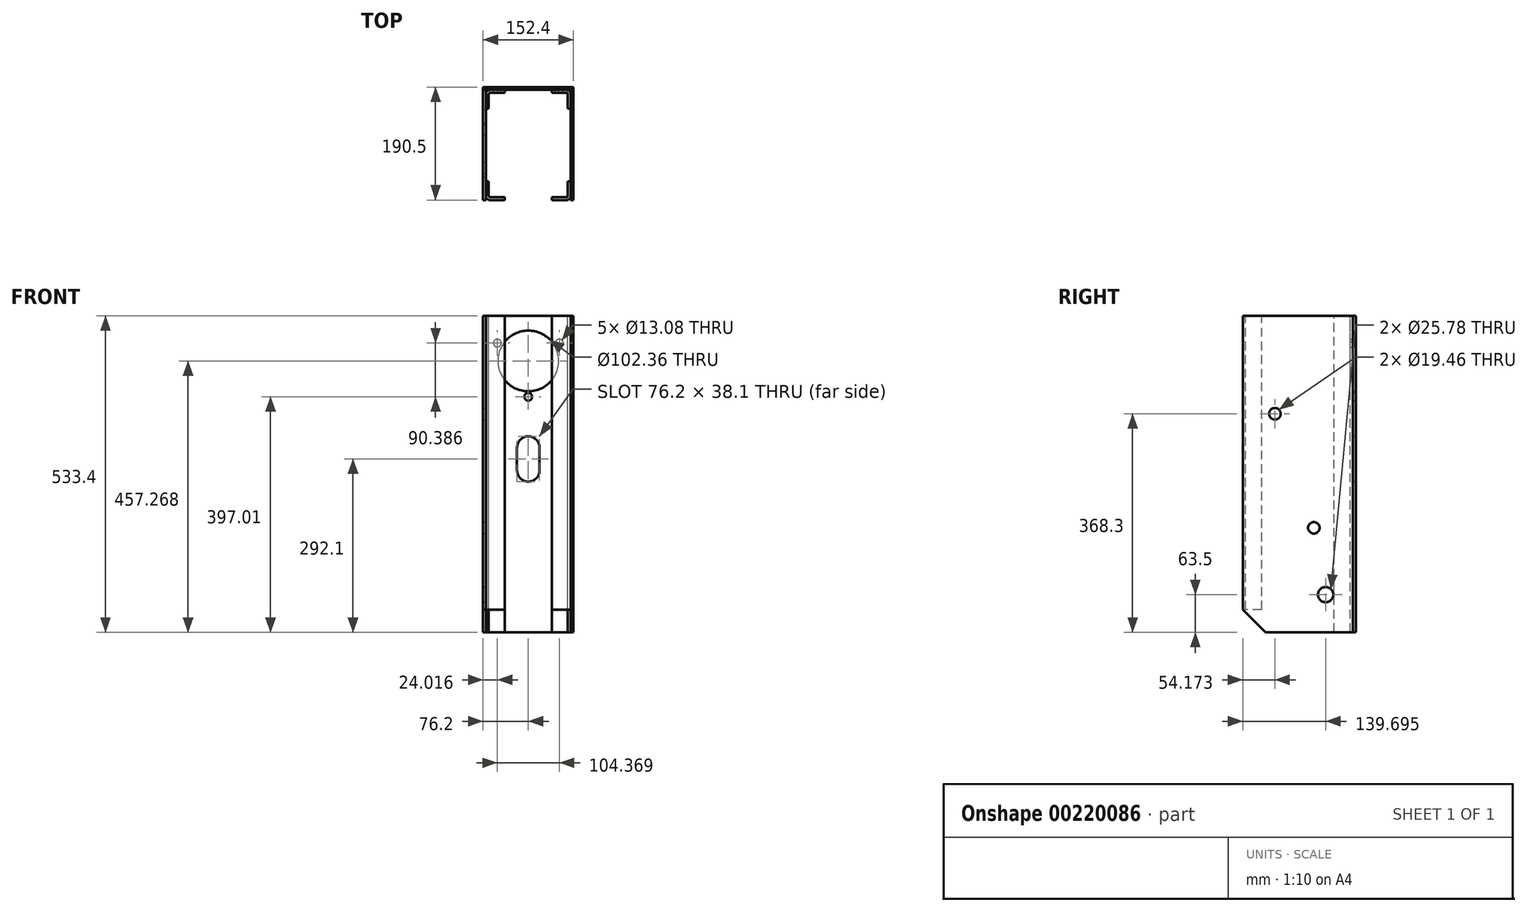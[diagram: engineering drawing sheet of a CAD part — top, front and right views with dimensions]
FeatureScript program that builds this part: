
annotation { "Feature Type Name" : "Feature", "Feature Type Description" : "" }
export const myFeature = defineFeature(function(context is Context, id is Id, definition is map)
    precondition{}
    {
        {
            var Q0;
            Q0=qCreatedBy(makeId("Front.planeOp"),FACE);
            var sketch = newSketch(context, id + "F0", { "sketchPlane" : qUnion([Q0])});
            skLineSegment(sketch, "E0.bottom", {"start": v(76.2, 266.7) * mm, "end": v(-76.2, 266.7) * mm});
            skLineSegment(sketch, "E0.top", {"start": v(76.2, -266.7) * mm, "end": v(-76.2, -266.7) * mm});
            skLineSegment(sketch, "E0.left", {"start": v(76.2, 266.7) * mm, "end": v(76.2, -266.7) * mm});
            skLineSegment(sketch, "E0.right", {"start": v(-76.2, 266.7) * mm, "end": v(-76.2, -266.7) * mm});
            skPoint(sketch, "E0.middle", {"position": v(0, 0) * mm});
            skSolve(sketch);
        }
        {
            var Q0;
            Q0 = qSketchRegion(id + "F0", true);
            extrude(context, id + "F1", {"entities" : qUnion([Q0]), "oppositeDirection" : true, "depth" : 4.78 * mm});
        }
        {
            var Q0;
            Q0=makeQuery(id+"F1.opExtrude","CAP_FACE",FACE,{"disambiguationData":[OSD([sQuery(id+"F0.wireOp",EDGE,"E0.bottom"),sQuery(id+"F0.wireOp",EDGE,"E0.top"),sQuery(id+"F0.wireOp",EDGE,"E0.left"),sQuery(id+"F0.wireOp",EDGE,"E0.right")])],"isStart":false});
            var sketch = newSketch(context, id + "F2", { "sketchPlane" : qUnion([Q0])});
            skLineSegment(sketch, "E1.0", {"start": v(-76.2, 266.7) * mm, "end": v(76.2, 266.7) * mm, "construction": true});
            skLineSegment(sketch, "E2", {"start": v(0, 0) * mm, "end": v(0, 190.57) * mm, "construction": true});
            skCircle(sketch, "E3", {"center": v(0, 190.57) * mm, "radius": 60.26 * mm, "construction": true});
            skCircle(sketch, "E4", {"center": v(0, 190.57) * mm, "radius": 51.18 * mm});
            skCircle(sketch, "E5", {"center": v(0, 130.31) * mm, "radius": 6.54 * mm});
            skCircle(sketch, "E6.1.0", {"center": v(52.18, 220.7) * mm, "radius": 6.54 * mm});
            skCircle(sketch, "E6.2.0", {"center": v(-52.18, 220.7) * mm, "radius": 6.54 * mm});
            skLineSegment(sketch, "E7", {"start": v(82.94, 251.81) * mm, "end": v(-98.55, 251.81) * mm, "construction": true});
            skSolve(sketch);
        }
        {
            var Q0;
            Q0 = qSketchRegion(id + "F2", true);
            extrude(context, id + "F3", {"entities" : qUnion([Q0]), "operationType" : NewBodyOperationType.REMOVE, "oppositeDirection" : true, "depth" : 25.4 * mm});
        }
        {
            var Q0;
            Q0=makeQuery(id+"F1.opExtrude","SWEPT_FACE",FACE,{"disambiguationData":[OSD([sQuery(id+"F0.wireOp",EDGE,"E0.bottom")])]});
            var sketch = newSketch(context, id + "F4", { "sketchPlane" : qUnion([Q0])});
            skLineSegment(sketch, "E8", {"start": v(76.2, 0) * mm, "end": v(76.2, -185.72) * mm});
            skLineSegment(sketch, "E9", {"start": v(71.42, 0) * mm, "end": v(71.42, -185.72) * mm});
            skLineSegment(sketch, "E10", {"start": v(76.2, -185.72) * mm, "end": v(71.42, -185.72) * mm});
            skLineSegment(sketch, "E11.MirrorCS", {"start": v(-71.42, 0) * mm, "end": v(-71.42, -185.72) * mm});
            skLineSegment(sketch, "E12.MirrorCS", {"start": v(-76.2, 0) * mm, "end": v(-76.2, -185.72) * mm});
            skLineSegment(sketch, "E13.MirrorCS", {"start": v(-76.2, -185.72) * mm, "end": v(-71.42, -185.72) * mm});
            skLineSegment(sketch, "E14.0", {"start": v(76.2, 0) * mm, "end": v(71.42, 0) * mm});
            skLineSegment(sketch, "E15.trimOffspring", {"start": v(-71.42, 0) * mm, "end": v(-76.2, 0) * mm});
            skPoint(sketch, "E16.end.orphan", {"position": v(76.2, 4.78) * mm});
            skPoint(sketch, "E16.start.orphan", {"position": v(71.42, 4.78) * mm});
            skPoint(sketch, "E17.orphan", {"position": v(-76.2, 4.78) * mm});
            skPoint(sketch, "E18.orphan", {"position": v(-71.42, 4.78) * mm});
            skSolve(sketch);
        }
        {
            var Q0;
            {var subQ3=sQuery(id+"F4.wireOp",EDGE,"E10");Q0=makeQuery(id+"F4.imprint","IMPRINT",FACE,{"disambiguationData":[TD([[makeQuery(id+"F4.imprint","IMPRINT",EDGE,{"derivedFrom":subQ3}),-1.0]])]});}
            var Q1;
            {var subQ0=sQuery(id+"F4.wireOp",EDGE,"E13.MirrorCS");Q1=makeQuery(id+"F4.imprint","IMPRINT",FACE,{"disambiguationData":[TD([[makeQuery(id+"F4.imprint","IMPRINT",EDGE,{"derivedFrom":subQ0}),1.0]])]});}
            var Q2;
            Q2=makeQuery(id+"F1.opExtrude","SWEPT_FACE",FACE,{"disambiguationData":[OSD([sQuery(id+"F0.wireOp",EDGE,"E0.top")])]});
            extrude(context, id + "F5", {"entities" : qUnion([Q0, Q1]), "endBound" : BoundingType.UP_TO_SURFACE, "oppositeDirection" : true, "endBoundEntityFace" : qUnion([Q2]), "depth" : 25.4 * mm});
        }
        {
            var Q0;
            Q0=makeQuery(id+"F1.opExtrude","SWEPT_FACE",FACE,{"disambiguationData":[OSD([sQuery(id+"F0.wireOp",EDGE,"E0.bottom")])]});
            var sketch = newSketch(context, id + "F6", { "sketchPlane" : qUnion([Q0])});
            skLineSegment(sketch, "E19.0", {"start": v(-71.42, 0) * mm, "end": v(-71.42, -31.75) * mm});
            skLineSegment(sketch, "E20.0", {"start": v(-39.67, 0) * mm, "end": v(-71.42, 0) * mm});
            skLineSegment(sketch, "E21.0", {"start": v(71.42, 0) * mm, "end": v(71.42, -31.75) * mm});
            skPoint(sketch, "E22.orphan", {"position": v(-76.2, 0) * mm});
            skPoint(sketch, "E23.orphan", {"position": v(76.2, 0) * mm});
            skLineSegment(sketch, "E24", {"start": v(-71.42, -185.72) * mm, "end": v(-39.67, -185.72) * mm});
            skLineSegment(sketch, "E25", {"start": v(-66.65, -180.95) * mm, "end": v(-66.65, -153.97) * mm});
            skLineSegment(sketch, "E26", {"start": v(-66.65, -4.78) * mm, "end": v(-39.67, -4.78) * mm});
            skLineSegment(sketch, "E27", {"start": v(66.65, -4.78) * mm, "end": v(66.65, -31.75) * mm});
            skLineSegment(sketch, "E28", {"start": v(66.65, -180.95) * mm, "end": v(39.67, -180.95) * mm});
            skLineSegment(sketch, "E29", {"start": v(-71.42, -153.97) * mm, "end": v(-66.65, -153.97) * mm});
            skLineSegment(sketch, "E30", {"start": v(-39.67, -180.95) * mm, "end": v(-39.67, -185.72) * mm});
            skLineSegment(sketch, "E31", {"start": v(-71.42, -31.75) * mm, "end": v(-66.65, -31.75) * mm});
            skLineSegment(sketch, "E32", {"start": v(-39.67, -4.78) * mm, "end": v(-39.67, 0) * mm});
            skLineSegment(sketch, "E33", {"start": v(39.67, 0) * mm, "end": v(39.67, -4.78) * mm});
            skLineSegment(sketch, "E34", {"start": v(66.65, -31.75) * mm, "end": v(71.42, -31.75) * mm});
            skLineSegment(sketch, "E35", {"start": v(39.67, -185.72) * mm, "end": v(39.67, -180.95) * mm});
            skLineSegment(sketch, "E36", {"start": v(66.65, -153.97) * mm, "end": v(71.42, -153.97) * mm});
            skLineSegment(sketch, "E37.trimOffspring", {"start": v(39.67, -4.78) * mm, "end": v(66.65, -4.78) * mm});
            skLineSegment(sketch, "E38.trimOffspring", {"start": v(66.65, -153.97) * mm, "end": v(66.65, -180.95) * mm});
            skLineSegment(sketch, "E39.trimOffspring", {"start": v(71.42, -153.97) * mm, "end": v(71.42, -185.72) * mm});
            skLineSegment(sketch, "E40.trimOffspring", {"start": v(-39.67, -180.95) * mm, "end": v(-66.65, -180.95) * mm});
            skLineSegment(sketch, "E41.trimOffspring", {"start": v(39.67, -185.72) * mm, "end": v(71.42, -185.72) * mm});
            skLineSegment(sketch, "E42.trimOffspring", {"start": v(-66.65, -31.75) * mm, "end": v(-66.65, -4.78) * mm});
            skLineSegment(sketch, "E43.trimOffspring", {"start": v(-71.42, -153.97) * mm, "end": v(-71.42, -185.72) * mm});
            skLineSegment(sketch, "E44", {"start": v(71.42, 0) * mm, "end": v(39.67, 0) * mm});
            skSolve(sketch);
        }
        {
            var Q0;
            Q0 = qSketchRegion(id + "F6", true);
            extrude(context, id + "F7", {"entities" : qUnion([Q0]), "oppositeDirection" : true, "depth" : 533.4 * mm});
        }
        {
            var Q0;
            Q0=makeQuery(id+"F7.opExtrude","SWEPT_EDGE",EDGE,{"disambiguationData":[OSD([sQuery(id+"F6.wireOp",EDGE,"E26"),sQuery(id+"F6.wireOp",EDGE,"E42.trimOffspring")])]});
            var Q1;
            Q1=makeQuery(id+"F7.opExtrude","SWEPT_EDGE",EDGE,{"disambiguationData":[OSD([sQuery(id+"F6.wireOp",EDGE,"E27"),sQuery(id+"F6.wireOp",EDGE,"E37.trimOffspring")])]});
            var Q2;
            Q2=makeQuery(id+"F7.opExtrude","SWEPT_EDGE",EDGE,{"disambiguationData":[OSD([sQuery(id+"F6.wireOp",EDGE,"E25"),sQuery(id+"F6.wireOp",EDGE,"E40.trimOffspring")])]});
            var Q3;
            Q3=makeQuery(id+"F7.opExtrude","SWEPT_EDGE",EDGE,{"disambiguationData":[OSD([sQuery(id+"F6.wireOp",EDGE,"E28"),sQuery(id+"F6.wireOp",EDGE,"E38.trimOffspring")])]});
            fillet(context, id + "F8", {"entities" : qUnion([Q0, Q1, Q2, Q3]), "radius" : 2.3 * mm, "tangentPropagation" : true, "allowEdgeOverflow" : false});
        }
        {
            var Q0;
            Q0=makeQuery(id+"F7.opExtrude","SWEPT_EDGE",EDGE,{"disambiguationData":[OSD([sQuery(id+"F0.wireOp",EDGE,"E0.bottom"),sQuery(id+"F6.wireOp",EDGE,"E21.0"),sQuery(id+"F6.wireOp",EDGE,"E44")])]});
            var Q1;
            Q1=makeQuery(id+"F7.opExtrude","SWEPT_EDGE",EDGE,{"disambiguationData":[OSD([sQuery(id+"F6.wireOp",EDGE,"E39.trimOffspring"),sQuery(id+"F6.wireOp",EDGE,"E41.trimOffspring")])]});
            var Q2;
            Q2=makeQuery(id+"F7.opExtrude","SWEPT_EDGE",EDGE,{"disambiguationData":[OSD([sQuery(id+"F6.wireOp",EDGE,"E24"),sQuery(id+"F6.wireOp",EDGE,"E43.trimOffspring")])]});
            var Q3;
            Q3=makeQuery(id+"F7.opExtrude","SWEPT_EDGE",EDGE,{"disambiguationData":[OSD([sQuery(id+"F0.wireOp",EDGE,"E0.bottom"),sQuery(id+"F6.wireOp",EDGE,"E19.0"),sQuery(id+"F6.wireOp",EDGE,"E20.0")])]});
            fillet(context, id + "F9", {"entities" : qUnion([Q0, Q1, Q2, Q3]), "radius" : 7.06 * mm, "tangentPropagation" : true, "allowEdgeOverflow" : false});
        }
        {
            var Q0;
            Q0=makeQuery(id+"F5.opExtrude","SWEPT_FACE",FACE,{"disambiguationData":[OSD([sQuery(id+"F4.wireOp",EDGE,"E8")])]});
            var sketch = newSketch(context, id + "F10", { "sketchPlane" : qUnion([Q0])});
            skLineSegment(sketch, "E45.0", {"start": v(-185.72, -266.7) * mm, "end": v(-185.72, 266.7) * mm, "construction": true});
            skLineSegment(sketch, "E46", {"start": v(-185.72, -203.2) * mm, "end": v(4.78, -203.2) * mm, "construction": true});
            skCircle(sketch, "E47", {"center": v(-46.02, -203.2) * mm, "radius": 12.9 * mm});
            skLineSegment(sketch, "E48.0", {"start": v(4.78, 266.7) * mm, "end": v(4.78, -266.7) * mm, "construction": true});
            skSolve(sketch);
        }
        {
            var Q0;
            Q0 = qSketchRegion(id + "F10", true);
            extrude(context, id + "F11", {"entities" : qUnion([Q0]), "operationType" : NewBodyOperationType.REMOVE, "endBound" : BoundingType.THROUGH_ALL, "oppositeDirection" : true, "depth" : 25.4 * mm});
        }
        {
            var Q0;
            Q0=makeQuery(id+"F5.boolean.opBoolean","MERGE",FACE,{"derivedFrom":[makeQuery(id+"F1.opExtrude","SWEPT_FACE",FACE,{"disambiguationData":[OSD([sQuery(id+"F0.wireOp",EDGE,"E0.left")])]}),makeQuery(id+"F5.opExtrude","SWEPT_FACE",FACE,{"disambiguationData":[OSD([sQuery(id+"F4.wireOp",EDGE,"E8")])]})]});
            var sketch = newSketch(context, id + "F12", { "sketchPlane" : qUnion([Q0])});
            skLineSegment(sketch, "E49", {"start": v(-46.02, -203.2) * mm, "end": v(-46.02, 0) * mm, "construction": true});
            skCircle(sketch, "E50", {"center": v(-46.02, -203.2) * mm, "radius": 114.3 * mm, "construction": true});
            skCircle(sketch, "E51.0", {"center": v(-46.02, -203.2) * mm, "radius": 12.9 * mm});
            skLineSegment(sketch, "E52.0", {"start": v(4.78, 266.7) * mm, "end": v(4.78, -266.7) * mm, "construction": true});
            skLineSegment(sketch, "E53", {"start": v(-46.02, -203.2) * mm, "end": v(-73.72, -46.11) * mm});
            skCircle(sketch, "E54", {"center": v(-65.87, -90.64) * mm, "radius": 9.72 * mm});
            skCircle(sketch, "E55", {"center": v(-46.02, -203.2) * mm, "radius": 203.2 * mm, "construction": true});
            skLineSegment(sketch, "E56", {"start": v(-141.27, 261.16) * mm, "end": v(-141.27, -53.14) * mm, "construction": true});
            skLineSegment(sketch, "E57.0", {"start": v(-185.72, -266.7) * mm, "end": v(-185.72, 266.7) * mm, "construction": true});
            skCircle(sketch, "E58", {"center": v(-131.55, 101.6) * mm, "radius": 9.73 * mm});
            skSolve(sketch);
        }
        {
            var Q0;
            Q0 = qSketchRegion(id + "F12", true);
            extrude(context, id + "F13", {"entities" : qUnion([Q0]), "operationType" : NewBodyOperationType.REMOVE, "endBound" : BoundingType.THROUGH_ALL, "oppositeDirection" : true, "depth" : 25.4 * mm});
        }
        {
            var Q0;
            Q0=makeQuery(id+"F7.opExtrude","SWEPT_FACE",FACE,{"disambiguationData":[OSD([sQuery(id+"F6.wireOp",EDGE,"E44")])]});
            var sketch = newSketch(context, id + "F14", { "sketchPlane" : qUnion([Q0])});
            skCircle(sketch, "E59.0", {"center": v(-52.18, 220.7) * mm, "radius": 6.54 * mm});
            skLineSegment(sketch, "E60.0", {"start": v(-39.67, 158.24) * mm, "end": v(-39.67, 222.9) * mm});
            skArc(sketch, "E61.0", {"start": v(39.67, 158.24) * mm, "mid": v(51.18, 190.57) * mm, "end": v(39.67, 222.9) * mm});
            skPoint(sketch, "E62.orphan", {"position": v(-39.67, 266.7) * mm});
            skPoint(sketch, "E63.orphan", {"position": v(-39.67, -266.7) * mm});
            skCircle(sketch, "E64.0", {"center": v(52.18, 220.7) * mm, "radius": 6.54 * mm});
            skLineSegment(sketch, "E65.0", {"start": v(39.67, 158.24) * mm, "end": v(39.67, 222.9) * mm});
            skPoint(sketch, "E66.orphan", {"position": v(39.67, 266.7) * mm});
            skPoint(sketch, "E67.orphan", {"position": v(39.67, -266.7) * mm});
            skArc(sketch, "E68.trimOffspring", {"start": v(-39.67, 222.9) * mm, "mid": v(-51.18, 190.57) * mm, "end": v(-39.67, 158.24) * mm});
            skSolve(sketch);
        }
        {
            var Q0;
            Q0 = qSketchRegion(id + "F14", true);
            extrude(context, id + "F15", {"entities" : qUnion([Q0]), "operationType" : NewBodyOperationType.REMOVE, "oppositeDirection" : true, "depth" : 6.35 * mm});
        }
        {
            var Q0;
            Q0=makeQuery(id+"F1.opExtrude","CAP_FACE",FACE,{"disambiguationData":[OSD([sQuery(id+"F0.wireOp",EDGE,"E0.bottom"),sQuery(id+"F0.wireOp",EDGE,"E0.top"),sQuery(id+"F0.wireOp",EDGE,"E0.left"),sQuery(id+"F0.wireOp",EDGE,"E0.right")])],"isStart":false});
            var sketch = newSketch(context, id + "F16", { "sketchPlane" : qUnion([Q0])});
            skCircle(sketch, "E69.0", {"center": v(0, 190.57) * mm, "radius": 51.18 * mm, "construction": true});
            skLineSegment(sketch, "E70", {"start": v(0, 190.57) * mm, "end": v(0, -139.77) * mm, "construction": true});
            skCircle(sketch, "E71", {"center": v(0, 25.4) * mm, "radius": 19.05 * mm, "construction": true});
            skArc(sketch, "E72", {"start": v(19.05, 44.45) * mm, "mid": v(0, 63.5) * mm, "end": v(-19.05, 44.45) * mm});
            skArc(sketch, "E73", {"start": v(-19.05, 6.35) * mm, "mid": v(0, -12.7) * mm, "end": v(19.05, 6.35) * mm});
            skLineSegment(sketch, "E74", {"start": v(-19.05, 44.45) * mm, "end": v(-19.05, 6.35) * mm});
            skLineSegment(sketch, "E75", {"start": v(19.05, 6.35) * mm, "end": v(19.05, 44.45) * mm});
            skSolve(sketch);
        }
        {
            var Q0;
            Q0 = qSketchRegion(id + "F16", true);
            extrude(context, id + "F17", {"entities" : qUnion([Q0]), "operationType" : NewBodyOperationType.REMOVE, "oppositeDirection" : true, "depth" : 6.35 * mm});
        }
        {
            var Q0;
            Q0=makeQuery(id+"F5.opExtrude","SWEPT_FACE",FACE,{"disambiguationData":[OSD([sQuery(id+"F4.wireOp",EDGE,"E8")])]});
            var sketch = newSketch(context, id + "F18", { "sketchPlane" : qUnion([Q0])});
            skLineSegment(sketch, "E76.0", {"start": v(-185.72, -266.7) * mm, "end": v(-185.72, -228.6) * mm});
            skLineSegment(sketch, "E77.0", {"start": v(-185.72, -266.7) * mm, "end": v(-147.62, -266.7) * mm});
            skLineSegment(sketch, "E78", {"start": v(-185.72, -228.6) * mm, "end": v(-147.62, -266.7) * mm});
            skPoint(sketch, "E79.orphan", {"position": v(0, -266.7) * mm});
            skPoint(sketch, "E80.orphan", {"position": v(-185.72, 266.7) * mm});
            skSolve(sketch);
        }
        {
            var Q0;
            Q0 = qSketchRegion(id + "F18", true);
            var Q1;
            Q1=makeQuery(id+"F5.opExtrude","SWEPT_FACE",FACE,{"disambiguationData":[OSD([sQuery(id+"F4.wireOp",EDGE,"E9")])]});
            extrude(context, id + "F19", {"entities" : qUnion([Q0]), "operationType" : NewBodyOperationType.REMOVE, "endBound" : BoundingType.UP_TO_SURFACE, "oppositeDirection" : true, "endBoundEntityFace" : qUnion([Q1]), "depth" : 25.4 * mm});
        }
        {
            var Q0;
            Q0=makeQuery(id+"F5.opExtrude","SWEPT_FACE",FACE,{"disambiguationData":[OSD([sQuery(id+"F4.wireOp",EDGE,"E12.MirrorCS")])]});
            var sketch = newSketch(context, id + "F20", { "sketchPlane" : qUnion([Q0])});
            skLineSegment(sketch, "E81.0", {"start": v(185.72, -266.7) * mm, "end": v(147.62, -266.7) * mm});
            skLineSegment(sketch, "E82.0", {"start": v(185.72, -266.7) * mm, "end": v(185.72, -228.6) * mm});
            skLineSegment(sketch, "E83", {"start": v(185.72, -228.6) * mm, "end": v(147.62, -266.7) * mm});
            skPoint(sketch, "E84.orphan", {"position": v(185.72, 266.7) * mm});
            skPoint(sketch, "E85.orphan", {"position": v(0, -266.7) * mm});
            skSolve(sketch);
        }
        {
            var Q0;
            Q0 = qSketchRegion(id + "F20", true);
            var Q1;
            Q1=makeQuery(id+"F5.opExtrude","SWEPT_FACE",FACE,{"disambiguationData":[OSD([sQuery(id+"F4.wireOp",EDGE,"E11.MirrorCS")])]});
            extrude(context, id + "F21", {"entities" : qUnion([Q0]), "operationType" : NewBodyOperationType.REMOVE, "endBound" : BoundingType.UP_TO_SURFACE, "oppositeDirection" : true, "endBoundEntityFace" : qUnion([Q1]), "depth" : 25.4 * mm});
        }
        {
            var Q0;
            Q0=makeQuery(id+"F7.opExtrude","CAP_FACE",FACE,{"disambiguationData":[OSD([sQuery(id+"F6.wireOp",EDGE,"E24"),sQuery(id+"F6.wireOp",EDGE,"E25"),sQuery(id+"F6.wireOp",EDGE,"E29"),sQuery(id+"F6.wireOp",EDGE,"E30"),sQuery(id+"F6.wireOp",EDGE,"E40.trimOffspring"),sQuery(id+"F6.wireOp",EDGE,"E43.trimOffspring")])],"isStart":false});
            var sketch = newSketch(context, id + "F22", { "sketchPlane" : qUnion([Q0])});
            skLineSegment(sketch, "E86.0.0", {"start": v(-39.67, 185.72) * mm, "end": v(-64.36, 185.72) * mm});
            skArc(sketch, "E86.0.1", {"start": v(-64.36, 185.72) * mm, "mid": v(-69.36, 183.66) * mm, "end": v(-71.42, 178.66) * mm});
            skLineSegment(sketch, "E86.0.2", {"start": v(-71.42, 178.66) * mm, "end": v(-71.42, 153.97) * mm});
            skLineSegment(sketch, "E86.0.3", {"start": v(-71.42, 153.97) * mm, "end": v(-66.65, 153.97) * mm});
            skLineSegment(sketch, "E86.0.4", {"start": v(-66.65, 153.97) * mm, "end": v(-66.65, 178.66) * mm});
            skArc(sketch, "E86.0.5", {"start": v(-66.65, 178.66) * mm, "mid": v(-65.98, 180.28) * mm, "end": v(-64.36, 180.95) * mm});
            skLineSegment(sketch, "E86.0.6", {"start": v(-64.36, 180.95) * mm, "end": v(-39.67, 180.95) * mm});
            skLineSegment(sketch, "E86.0.7", {"start": v(-39.67, 180.95) * mm, "end": v(-39.67, 185.72) * mm});
            skLineSegment(sketch, "E87.0.0", {"start": v(71.42, 153.97) * mm, "end": v(71.42, 178.66) * mm});
            skArc(sketch, "E87.0.1", {"start": v(71.42, 178.66) * mm, "mid": v(69.36, 183.66) * mm, "end": v(64.36, 185.72) * mm});
            skLineSegment(sketch, "E87.0.2", {"start": v(64.36, 185.72) * mm, "end": v(39.67, 185.72) * mm});
            skLineSegment(sketch, "E87.0.3", {"start": v(39.67, 185.72) * mm, "end": v(39.67, 180.95) * mm});
            skLineSegment(sketch, "E87.0.4", {"start": v(39.67, 180.95) * mm, "end": v(64.36, 180.95) * mm});
            skArc(sketch, "E87.0.5", {"start": v(64.36, 180.95) * mm, "mid": v(65.98, 180.28) * mm, "end": v(66.65, 178.66) * mm});
            skLineSegment(sketch, "E87.0.6", {"start": v(66.65, 178.66) * mm, "end": v(66.65, 153.97) * mm});
            skLineSegment(sketch, "E87.0.7", {"start": v(66.65, 153.97) * mm, "end": v(71.42, 153.97) * mm});
            skSolve(sketch);
        }
        {
            var Q0;
            Q0 = qSketchRegion(id + "F22", true);
            extrude(context, id + "F23", {"entities" : qUnion([Q0]), "operationType" : NewBodyOperationType.REMOVE, "oppositeDirection" : true, "depth" : 38.1 * mm});
        }
    });
